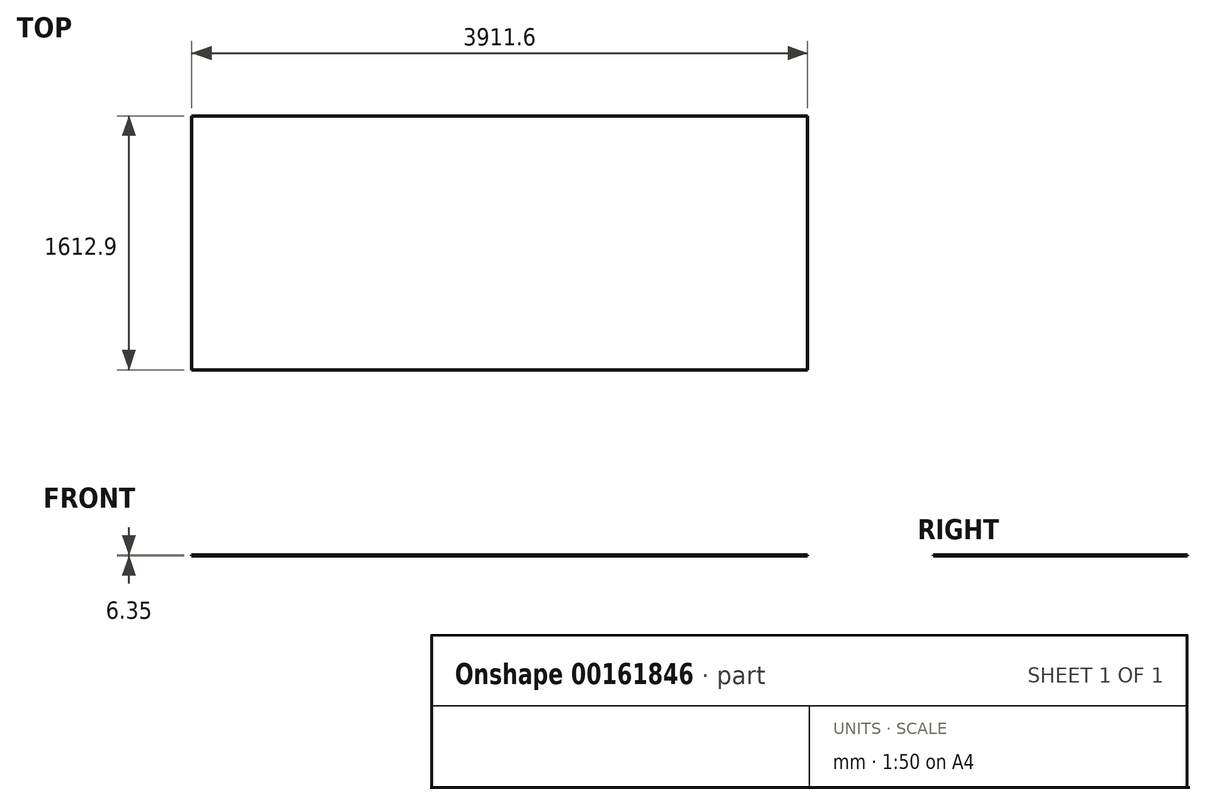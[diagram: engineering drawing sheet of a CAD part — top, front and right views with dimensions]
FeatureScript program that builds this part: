
annotation { "Feature Type Name" : "Feature", "Feature Type Description" : "" }
export const myFeature = defineFeature(function(context is Context, id is Id, definition is map)
    precondition{}
    {
        {
            var Q0;
            Q0=qCreatedBy(makeId("Top.planeOp"),FACE);
            var sketch = newSketch(context, id + "F0", { "sketchPlane" : qUnion([Q0])});
            skLineSegment(sketch, "E0.bottom", {"start": v(-1955.8, 806.45) * mm, "end": v(1955.8, 806.45) * mm});
            skLineSegment(sketch, "E0.top", {"start": v(-1955.8, -806.45) * mm, "end": v(1955.8, -806.45) * mm});
            skLineSegment(sketch, "E0.left", {"start": v(-1955.8, 806.45) * mm, "end": v(-1955.8, -806.45) * mm});
            skLineSegment(sketch, "E0.right", {"start": v(1955.8, 806.45) * mm, "end": v(1955.8, -806.45) * mm});
            skPoint(sketch, "E0.middle", {"position": v(0, 0) * mm});
            skSolve(sketch);
        }
        {
            var Q0;
            Q0 = qSketchRegion(id + "F0", true);
            extrude(context, id + "F1", {"entities" : qUnion([Q0]), "depth" : 6.35 * mm});
        }
    });
